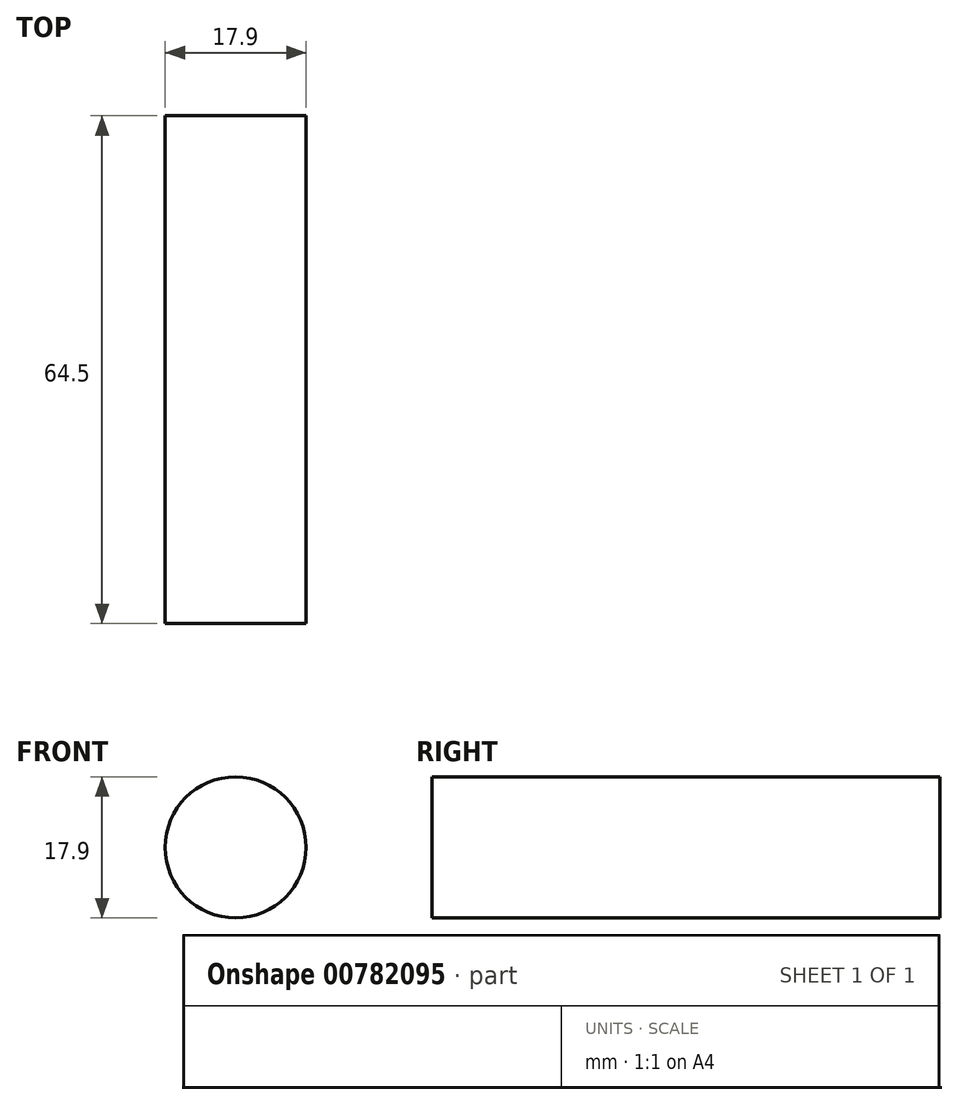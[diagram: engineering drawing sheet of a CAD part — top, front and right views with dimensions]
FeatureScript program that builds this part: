
annotation { "Feature Type Name" : "Feature", "Feature Type Description" : "" }
export const myFeature = defineFeature(function(context is Context, id is Id, definition is map)
    precondition{}
    {
        {
            var Q0;
            Q0=qCreatedBy(makeId("Front.planeOp"),FACE);
            var sketch = newSketch(context, id + "F0", { "sketchPlane" : qUnion([Q0])});
            skCircle(sketch, "E0", {"center": v(0, 0) * mm, "radius": 8.95 * mm});
            skSolve(sketch);
        }
        {
            var Q0;
            Q0 = qSketchRegion(id + "F0", true);
            extrude(context, id + "F1", {"entities" : qUnion([Q0]), "depth" : 64.5 * mm, "offsetDistance" : 25 * mm});
        }
    });
